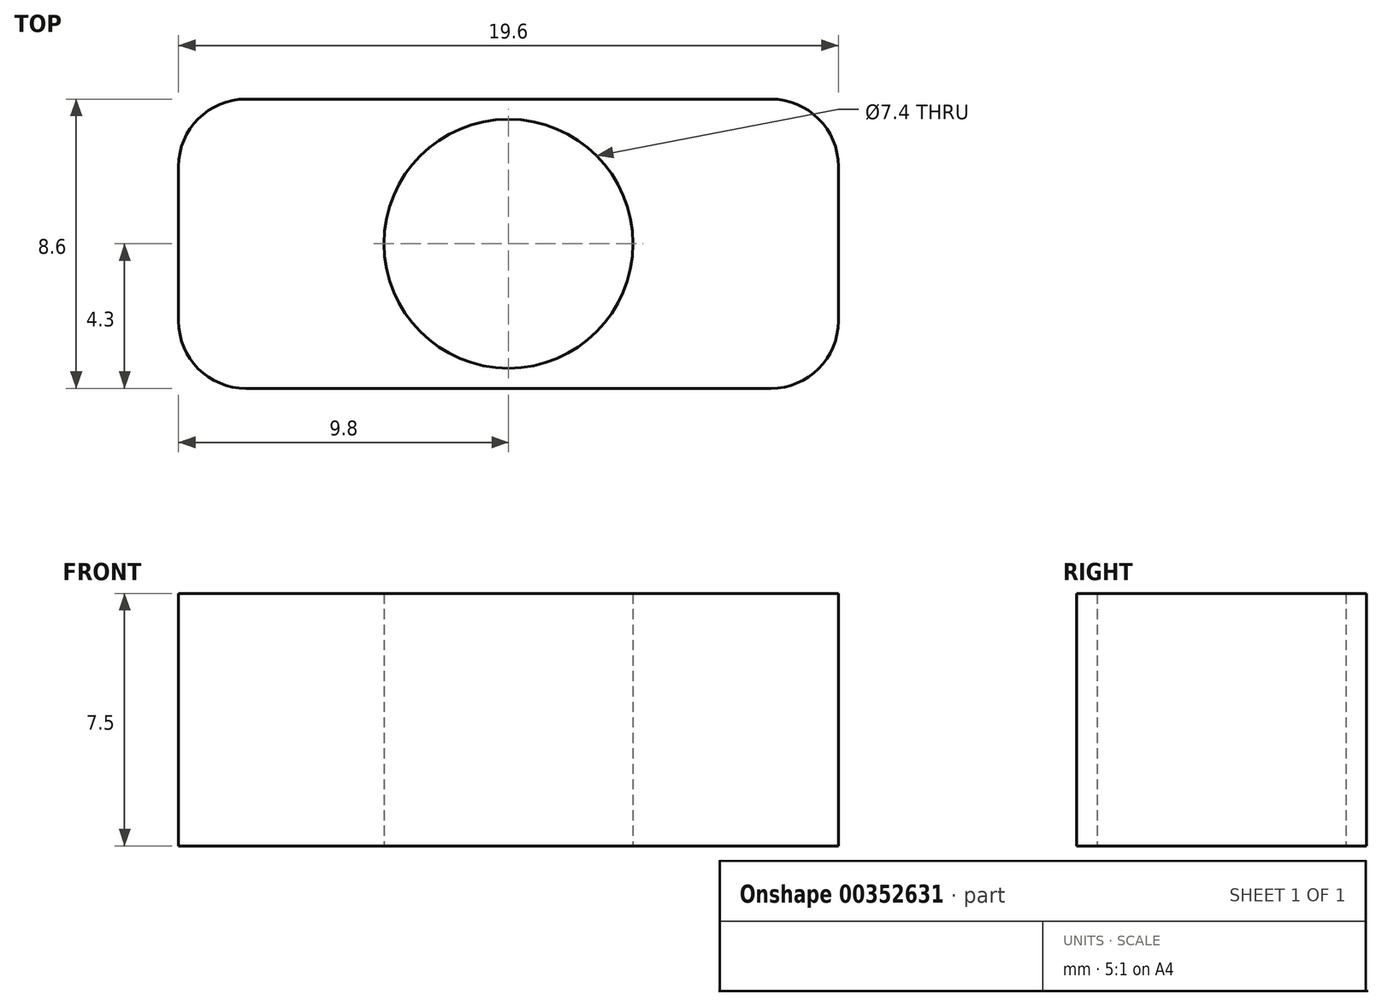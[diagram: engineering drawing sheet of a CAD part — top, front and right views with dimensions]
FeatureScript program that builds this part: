
annotation { "Feature Type Name" : "Feature", "Feature Type Description" : "" }
export const myFeature = defineFeature(function(context is Context, id is Id, definition is map)
    precondition{}
    {
        {
            var Q0;
            Q0=qCreatedBy(makeId("Top.planeOp"),FACE);
            var sketch = newSketch(context, id + "F0", { "sketchPlane" : qUnion([Q0])});
            skLineSegment(sketch, "E0.bottom", {"start": v(0, 0) * mm, "end": v(19.6, 0) * mm});
            skLineSegment(sketch, "E0.top", {"start": v(0, 8.6) * mm, "end": v(19.6, 8.6) * mm});
            skLineSegment(sketch, "E0.left", {"start": v(0, 0) * mm, "end": v(0, 8.6) * mm});
            skLineSegment(sketch, "E0.right", {"start": v(19.6, 0) * mm, "end": v(19.6, 8.6) * mm});
            skLineSegment(sketch, "E1", {"start": v(19.6, 4.3) * mm, "end": v(0, 4.3) * mm, "construction": true});
            skLineSegment(sketch, "E2", {"start": v(9.8, 0) * mm, "end": v(9.8, 8.6) * mm, "construction": true});
            skPoint(sketch, "E3", {"position": v(9.8, 4.3) * mm});
            skCircle(sketch, "E4", {"center": v(9.8, 4.3) * mm, "radius": 3.7 * mm});
            skSolve(sketch);
        }
        {
            var Q0;
            Q0=makeQuery(id+"F0.imprint","IMPRINT",FACE,{"disambiguationData":[TD([[makeQuery(id+"F0.imprint","IMPRINT",EDGE,{"derivedFrom":sQuery(id+"F0.wireOp",EDGE,"E0.bottom")}),1.0]])]});
            extrude(context, id + "F1", {"entities" : qUnion([Q0]), "depth" : 7.5 * mm});
        }
        {
            var Q0;
            Q0=makeQuery(id+"F1.opExtrude","SWEPT_EDGE",EDGE,{"disambiguationData":[OSD([sQuery(id+"F0.wireOp",EDGE,"E0.bottom"),sQuery(id+"F0.wireOp",EDGE,"E0.left")])]});
            var Q1;
            Q1=makeQuery(id+"F1.opExtrude","SWEPT_EDGE",EDGE,{"disambiguationData":[OSD([sQuery(id+"F0.wireOp",EDGE,"E0.bottom"),sQuery(id+"F0.wireOp",EDGE,"E0.right")])]});
            var Q2;
            Q2=makeQuery(id+"F1.opExtrude","SWEPT_EDGE",EDGE,{"disambiguationData":[OSD([sQuery(id+"F0.wireOp",EDGE,"E0.top"),sQuery(id+"F0.wireOp",EDGE,"E0.left")])]});
            var Q3;
            Q3=makeQuery(id+"F1.opExtrude","SWEPT_EDGE",EDGE,{"disambiguationData":[OSD([sQuery(id+"F0.wireOp",EDGE,"E0.top"),sQuery(id+"F0.wireOp",EDGE,"E0.right")])]});
            fillet(context, id + "F2", {"entities" : qUnion([Q0, Q1, Q2, Q3]), "radius" : 2 * mm, "tangentPropagation" : true, "allowEdgeOverflow" : false});
        }
    });
